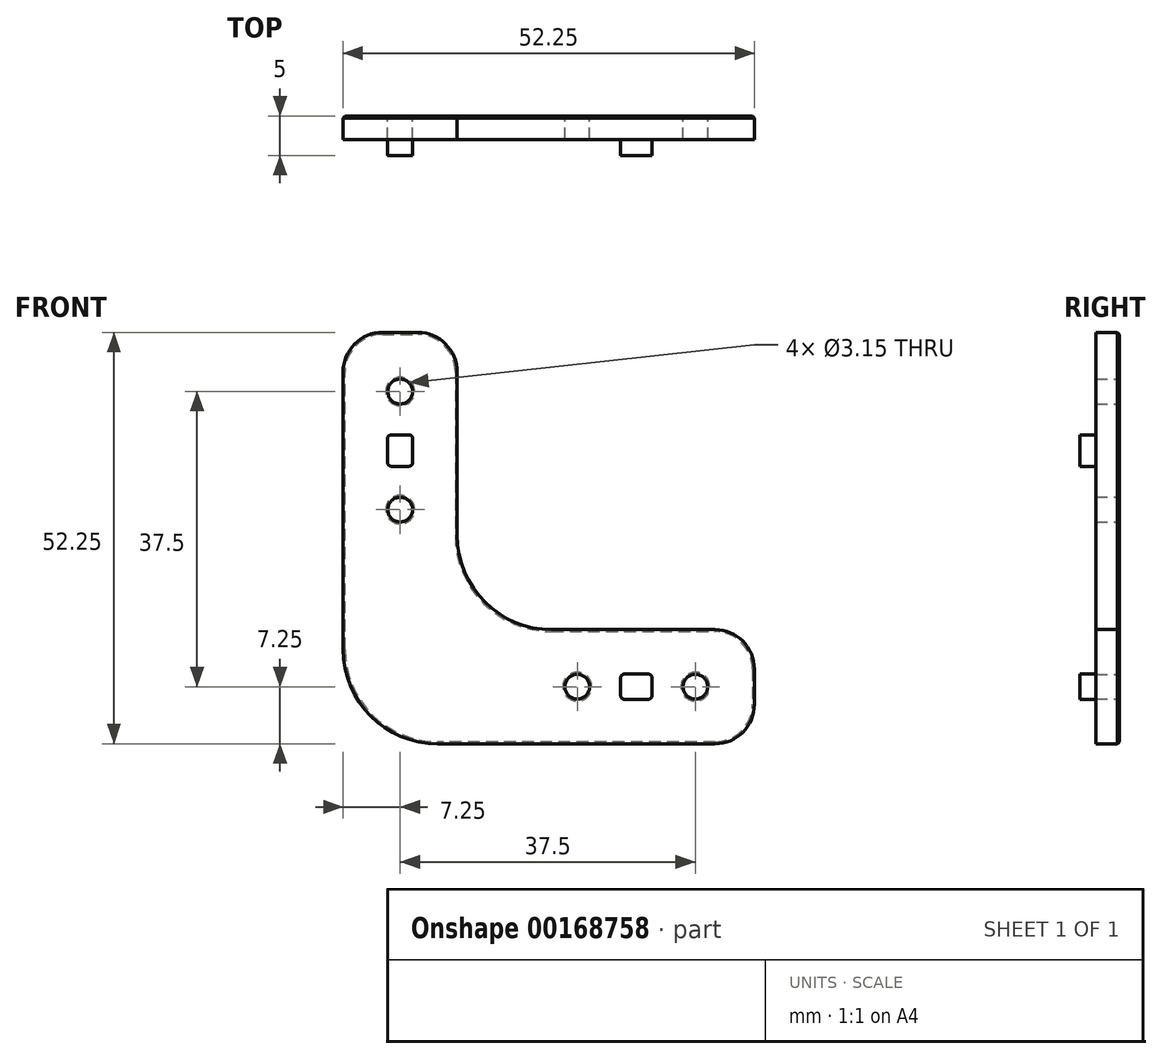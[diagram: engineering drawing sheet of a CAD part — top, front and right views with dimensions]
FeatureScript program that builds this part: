
annotation { "Feature Type Name" : "Feature", "Feature Type Description" : "" }
export const myFeature = defineFeature(function(context is Context, id is Id, definition is map)
    precondition{}
    {
        {
            var Q0;
            Q0=qCreatedBy(makeId("Front.planeOp"),FACE);
            var sketch = newSketch(context, id + "F0", { "sketchPlane" : qUnion([Q0])});
            skLineSegment(sketch, "E0", {"start": v(0, 45) * mm, "end": v(0, 0) * mm, "construction": true});
            skLineSegment(sketch, "E1", {"start": v(0, 0) * mm, "end": v(45, 0) * mm, "construction": true});
            skLineSegment(sketch, "E2", {"start": v(7.25, 45) * mm, "end": v(-7.25, 45) * mm});
            skLineSegment(sketch, "E3", {"start": v(-7.25, 45) * mm, "end": v(-7.25, -7.25) * mm});
            skLineSegment(sketch, "E4", {"start": v(-7.25, -7.25) * mm, "end": v(45, -7.25) * mm});
            skLineSegment(sketch, "E5", {"start": v(45, -7.25) * mm, "end": v(45, 7.25) * mm});
            skLineSegment(sketch, "E6", {"start": v(45, 7.25) * mm, "end": v(7.25, 7.25) * mm});
            skLineSegment(sketch, "E7", {"start": v(7.25, 7.25) * mm, "end": v(7.25, 45) * mm});
            skCircle(sketch, "E8", {"center": v(0, 37.5) * mm, "radius": 1.57 * mm});
            skCircle(sketch, "E9", {"center": v(0, 22.5) * mm, "radius": 1.57 * mm});
            skCircle(sketch, "E10", {"center": v(37.5, 0) * mm, "radius": 1.57 * mm});
            skCircle(sketch, "E11", {"center": v(22.5, 0) * mm, "radius": 1.57 * mm});
            skSolve(sketch);
        }
        {
            var Q0;
            Q0=makeQuery(id+"F0.imprint","IMPRINT",FACE,{"disambiguationData":[TD([[makeQuery(id+"F0.imprint","IMPRINT",EDGE,{"derivedFrom":sQuery(id+"F0.wireOp",EDGE,"E2")}),1.0]])]});
            extrude(context, id + "F1", {"entities" : qUnion([Q0]), "depth" : 3 * mm});
        }
        {
            var Q0;
            Q0=makeQuery(id+"F1.opExtrude","SWEPT_EDGE",EDGE,{"disambiguationData":[OSD([sQuery(id+"F0.wireOp",EDGE,"E2"),sQuery(id+"F0.wireOp",EDGE,"E3")])]});
            var Q1;
            Q1=makeQuery(id+"F1.opExtrude","SWEPT_EDGE",EDGE,{"disambiguationData":[OSD([sQuery(id+"F0.wireOp",EDGE,"E2"),sQuery(id+"F0.wireOp",EDGE,"E7")])]});
            var Q2;
            Q2=makeQuery(id+"F1.opExtrude","SWEPT_EDGE",EDGE,{"disambiguationData":[OSD([sQuery(id+"F0.wireOp",EDGE,"E5"),sQuery(id+"F0.wireOp",EDGE,"E6")])]});
            var Q3;
            Q3=makeQuery(id+"F1.opExtrude","SWEPT_EDGE",EDGE,{"disambiguationData":[OSD([sQuery(id+"F0.wireOp",EDGE,"E4"),sQuery(id+"F0.wireOp",EDGE,"E5")])]});
            fillet(context, id + "F2", {"entities" : qUnion([Q0, Q1, Q2, Q3]), "radius" : 5 * mm, "allowEdgeOverflow" : false});
        }
        {
            var Q0;
            Q0=makeQuery(id+"F1.opExtrude","SWEPT_EDGE",EDGE,{"disambiguationData":[OSD([sQuery(id+"F0.wireOp",EDGE,"E6"),sQuery(id+"F0.wireOp",EDGE,"E7")])]});
            var Q1;
            Q1=makeQuery(id+"F1.opExtrude","SWEPT_EDGE",EDGE,{"disambiguationData":[OSD([sQuery(id+"F0.wireOp",EDGE,"E3"),sQuery(id+"F0.wireOp",EDGE,"E4")])]});
            fillet(context, id + "F3", {"entities" : qUnion([Q0, Q1]), "radius" : 12 * mm, "allowEdgeOverflow" : false});
        }
        {
            var Q0;
            Q0=makeQuery(id+"F1.opExtrude","CAP_FACE",FACE,{"disambiguationData":[OSD([sQuery(id+"F0.wireOp",EDGE,"E2"),sQuery(id+"F0.wireOp",EDGE,"E3"),sQuery(id+"F0.wireOp",EDGE,"E4"),sQuery(id+"F0.wireOp",EDGE,"E5"),sQuery(id+"F0.wireOp",EDGE,"E6"),sQuery(id+"F0.wireOp",EDGE,"E7"),sQuery(id+"F0.wireOp",EDGE,"E8"),sQuery(id+"F0.wireOp",EDGE,"E9"),sQuery(id+"F0.wireOp",EDGE,"E10"),sQuery(id+"F0.wireOp",EDGE,"E11")])],"isStart":false});
            var sketch = newSketch(context, id + "F4", { "sketchPlane" : qUnion([Q0])});
            skCircle(sketch, "E12.0", {"center": v(0, 37.5) * mm, "radius": 1.57 * mm, "construction": true});
            skCircle(sketch, "E12.1", {"center": v(0, 22.5) * mm, "radius": 1.57 * mm, "construction": true});
            skCircle(sketch, "E12.2", {"center": v(22.5, 0) * mm, "radius": 1.57 * mm, "construction": true});
            skCircle(sketch, "E12.3", {"center": v(37.5, 0) * mm, "radius": 1.57 * mm, "construction": true});
            skLineSegment(sketch, "E13", {"start": v(0, 37.5) * mm, "end": v(0, 22.5) * mm, "construction": true});
            skLineSegment(sketch, "E14", {"start": v(37.5, 0) * mm, "end": v(22.5, 0) * mm, "construction": true});
            skLineSegment(sketch, "E15.bottom", {"start": v(1.6, 32) * mm, "end": v(-1.6, 32) * mm});
            skLineSegment(sketch, "E15.top", {"start": v(1.6, 28) * mm, "end": v(-1.6, 28) * mm});
            skLineSegment(sketch, "E15.left", {"start": v(1.6, 32) * mm, "end": v(1.6, 28) * mm});
            skLineSegment(sketch, "E15.right", {"start": v(-1.6, 32) * mm, "end": v(-1.6, 28) * mm});
            skPoint(sketch, "E15.middle", {"position": v(0, 30) * mm});
            skLineSegment(sketch, "E16.bottom", {"start": v(32, 1.6) * mm, "end": v(28, 1.6) * mm});
            skLineSegment(sketch, "E16.top", {"start": v(32, -1.6) * mm, "end": v(28, -1.6) * mm});
            skLineSegment(sketch, "E16.left", {"start": v(32, 1.6) * mm, "end": v(32, -1.6) * mm});
            skLineSegment(sketch, "E16.right", {"start": v(28, 1.6) * mm, "end": v(28, -1.6) * mm});
            skPoint(sketch, "E16.middle", {"position": v(30, 0) * mm});
            skSolve(sketch);
        }
        {
            var Q0;
            Q0 = qSketchRegion(id + "F4", true);
            extrude(context, id + "F5", {"entities" : qUnion([Q0]), "operationType" : NewBodyOperationType.ADD, "depth" : 2 * mm});
        }
        {
            var Q0;
            Q0=makeQuery(id+"F5.opExtrude","SWEPT_EDGE",EDGE,{"disambiguationData":[OSD([sQuery(id+"F4.wireOp",EDGE,"E16.top"),sQuery(id+"F4.wireOp",EDGE,"E16.right")])]});
            var Q1;
            Q1=makeQuery(id+"F5.opExtrude","SWEPT_EDGE",EDGE,{"disambiguationData":[OSD([sQuery(id+"F4.wireOp",EDGE,"E16.top"),sQuery(id+"F4.wireOp",EDGE,"E16.left")])]});
            var Q2;
            Q2=makeQuery(id+"F5.opExtrude","SWEPT_EDGE",EDGE,{"disambiguationData":[OSD([sQuery(id+"F4.wireOp",EDGE,"E16.bottom"),sQuery(id+"F4.wireOp",EDGE,"E16.left")])]});
            var Q3;
            Q3=makeQuery(id+"F5.opExtrude","SWEPT_EDGE",EDGE,{"disambiguationData":[OSD([sQuery(id+"F4.wireOp",EDGE,"E16.bottom"),sQuery(id+"F4.wireOp",EDGE,"E16.right")])]});
            var Q4;
            Q4=makeQuery(id+"F5.opExtrude","SWEPT_EDGE",EDGE,{"disambiguationData":[OSD([sQuery(id+"F4.wireOp",EDGE,"E15.top"),sQuery(id+"F4.wireOp",EDGE,"E15.right")])]});
            var Q5;
            Q5=makeQuery(id+"F5.opExtrude","SWEPT_EDGE",EDGE,{"disambiguationData":[OSD([sQuery(id+"F4.wireOp",EDGE,"E15.bottom"),sQuery(id+"F4.wireOp",EDGE,"E15.right")])]});
            var Q6;
            Q6=makeQuery(id+"F5.opExtrude","SWEPT_EDGE",EDGE,{"disambiguationData":[OSD([sQuery(id+"F4.wireOp",EDGE,"E15.top"),sQuery(id+"F4.wireOp",EDGE,"E15.left")])]});
            var Q7;
            Q7=makeQuery(id+"F5.opExtrude","SWEPT_EDGE",EDGE,{"disambiguationData":[OSD([sQuery(id+"F4.wireOp",EDGE,"E15.bottom"),sQuery(id+"F4.wireOp",EDGE,"E15.left")])]});
            fillet(context, id + "F6", {"entities" : qUnion([Q0, Q1, Q2, Q3, Q4, Q5, Q6, Q7]), "radius" : 0.5 * mm, "allowEdgeOverflow" : false});
        }
        {
            var Q0;
            Q0=makeQuery(id+"F1.opExtrude","CAP_FACE",FACE,{"disambiguationData":[OSD([sQuery(id+"F0.wireOp",EDGE,"E2"),sQuery(id+"F0.wireOp",EDGE,"E3"),sQuery(id+"F0.wireOp",EDGE,"E4"),sQuery(id+"F0.wireOp",EDGE,"E5"),sQuery(id+"F0.wireOp",EDGE,"E6"),sQuery(id+"F0.wireOp",EDGE,"E7"),sQuery(id+"F0.wireOp",EDGE,"E8"),sQuery(id+"F0.wireOp",EDGE,"E9"),sQuery(id+"F0.wireOp",EDGE,"E10"),sQuery(id+"F0.wireOp",EDGE,"E11")])],"isStart":true});
            chamfer(context, id + "F7", {"entities" : qUnion([Q0]), "width" : 0.25 * mm});
        }
    });
